# Revit family: Trim-Waterworks-Flyte-Volume_Control
name_source: partatom
category: Plumbing Fixtures
revit_build: Autodesk Revit MEP 2014 (Build: 20140709_2115(x64)
units: mm (PartAtom-declared; Revit-internal decimal feet)

## types (8) — shared parameters
ADA Compliant = Yes
Anti-scald Protection = No
Assembly Code = D2010
CW Connection = Yes
Certification IAPMO = Yes
Certification State of MA = Yes
Certification cUPC = Yes
Control Valve Rough-in Depth Maximum = 0' - 4 1/4"
Control Valve Rough-in Depth Minimum = 0' - 3 1/4"
Default Elevation = 2' - 10"
Depth = 0' - 2 5/16"
Fittings Hole Diameter = 0' - 1 3/8"
HW Connection = Yes
Hot Limit Safety Stop = No
Keynote = 22 40 00
Length = 0' - 2 3/8"
Manufacturer = Waterworks
Product Documentation Link = http://assets.waterworks.com
Product Page URL = http://www.waterworks.com
URL = http://www.waterworks.com
Vent Connection = No
Version = 2014 - v1.0a
Warranty = http://www.waterworks.com
Waste Connection = No
‌Installation Requirements or Notes = Required 1/2'' valve rough Hot -GUVC18 or Cold -GUVC19, sold separately.
zero-valued in all types: CWFU, HWFU, WFU

## per-type parameters (varying)
| type | Code Compliance | Constraint | ControlM | Cross Handles | Description | Finish | Height | Lever Handles | Model | Model SKU | Product Name |
| Lever Handle - Chrome | Code # FLSV50: Complies with ASME A112.18.1/CSA B125.1, ASTM E 1621-05, ANSI A117.1 ADA.   Certified with IAPMO, cUPC & State of MA | 1 | 1 | No | Flyte Volume Control Valve Trim with Metal Lever Handle in Chrome | Metal - Waterworks - Chrome | 0' - 4 5/16" | Yes | FLVC50 | 05-96038-75510 | Flyte Volume Control Valve Trim with Metal Lever Handle |
| Lever Handle - Graphite | Code # FLSV50: Complies with ASME A112.18.1/CSA B125.1, ASTM E 1621-05, ANSI A117.1 ADA.   Certified with IAPMO, cUPC & State of MA | 1 | 2 | No | Flyte Volume Control Valve Trim with Metal Lever Handle in Graphite | Metal - Waterworks - Graphite | 0' - 4 5/16" | Yes | FLVC50 | 05-58938-50372 | Flyte Volume Control Valve Trim with Metal Lever Handle |
| Lever Handle - Nickel | Code # FLSV50: Complies with ASME A112.18.1/CSA B125.1, ASTM E 1621-05, ANSI A117.1 ADA.   Certified with IAPMO, cUPC & State of MA | 1 | 3 | No | Flyte Volume Control Valve Trim with Metal Lever Handle in Nickel | Metal - Waterworks - Nickel | 0' - 4 5/16" | Yes | FLVC50 | 05-82622-50145 | Flyte Volume Control Valve Trim with Metal Lever Handle |
| Lever Handle - Unlacquered Brass | Code # FLSV50: Complies with ASME A112.18.1/CSA B125.1, ASTM E 1621-05, ANSI A117.1 ADA.   Certified with IAPMO, cUPC & State of MA | 1 | 4 | No | Flyte Volume Control Valve Trim with Metal Lever Handle in Unlacquered Brass | Metal - Waterworks - Unlacquered Brass | 0' - 4 5/16" | Yes | FLVC50 | 05-54097-90511 | Flyte Volume Control Valve Trim with Metal Lever Handle |
| Cross Handle - Chrome | Code # FLSV40: | 2 | 5 | Yes | Flyte Volume Control Valve Trim with Metal Cross Handle in Chrome | Metal - Waterworks - Chrome | 0' - 2 3/8" | No | FLVC40 | 05-66137-92977 | Flyte Volume Control Valve Trim with Metal Cross Handle |
| Cross Handle - Graphite | Code # FLSV40: | 2 | 6 | Yes | Flyte Volume Control Valve Trim with Metal Cross Handle in Graphite | Metal - Waterworks - Graphite | 0' - 2 3/8" | No | FLVC40 | 05-87745-21106 | Flyte Volume Control Valve Trim with Metal Cross Handle |
| Cross Handle - Nickel | Code # FLSV40: | 2 | 7 | Yes | Flyte Volume Control Valve Trim with Metal Cross Handle in Nickel | Metal - Waterworks - Nickel | 0' - 2 3/8" | No | FLVC40 | 05-63184-81440 | Flyte Volume Control Valve Trim with Metal Cross Handle |
| Cross Handle - Unlacquered Brass | Code # FLSV40: | 2 | 8 | Yes | Flyte Volume Control Valve Trim with Metal Cross Handle in Unlacquered Brass | Metal - Waterworks - Unlacquered Brass | 0' - 2 3/8" | No | FLVC40 | 05-56007-64486 | Flyte Volume Control Valve Trim with Metal Cross Handle |

## geometry (parser evidence)
native form markers: Sweep x3
no freeform markers — native parametric forms only
